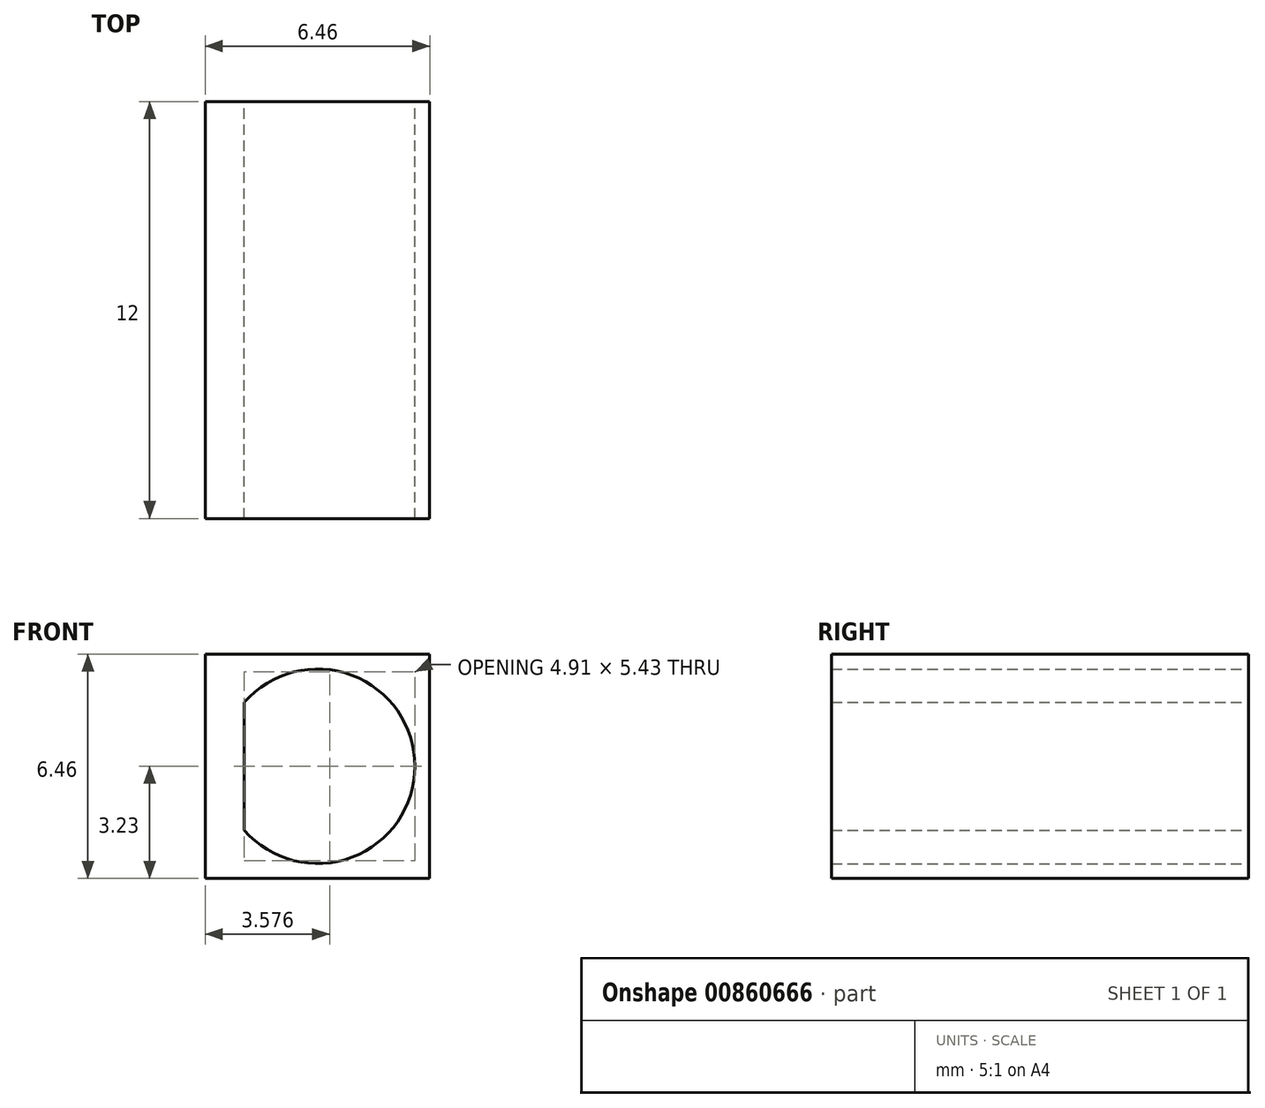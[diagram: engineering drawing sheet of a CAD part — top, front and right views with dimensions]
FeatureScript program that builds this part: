
annotation { "Feature Type Name" : "Feature", "Feature Type Description" : "" }
export const myFeature = defineFeature(function(context is Context, id is Id, definition is map)
    precondition{}
    {
        {
            var Q0;
            Q0=qCreatedBy(makeId("Front.planeOp"),FACE);
            var sketch = newSketch(context, id + "F0", { "sketchPlane" : qUnion([Q0])});
            skLineSegment(sketch, "E0.bottom", {"start": v(3.23, 3.23) * mm, "end": v(-3.23, 3.23) * mm});
            skLineSegment(sketch, "E0.top", {"start": v(3.23, -3.23) * mm, "end": v(-3.23, -3.23) * mm});
            skLineSegment(sketch, "E0.left", {"start": v(3.23, 3.23) * mm, "end": v(3.23, -3.23) * mm});
            skLineSegment(sketch, "E0.right", {"start": v(-3.23, 3.23) * mm, "end": v(-3.23, -3.23) * mm});
            skPoint(sketch, "E0.middle", {"position": v(0, 0) * mm});
            skSolve(sketch);
        }
        {
            var Q0;
            Q0=qCreatedBy(makeId("Front.planeOp"),FACE);
            var sketch = newSketch(context, id + "F1", { "sketchPlane" : qUnion([Q0])});
            skCircle(sketch, "E1", {"center": v(0, 0) * mm, "radius": 2.8 * mm});
            skSolve(sketch);
        }
        {
            var Q0;
            Q0 = qSketchRegion(id + "F0", true);
            extrude(context, id + "F2", {"entities" : qUnion([Q0]), "depth" : 12 * mm, "offsetDistance" : 25.4 * mm});
        }
        {
            var Q0;
            Q0 = qSketchRegion(id + "F1", true);
            extrude(context, id + "F3", {"entities" : qUnion([Q0]), "operationType" : NewBodyOperationType.REMOVE, "depth" : 12 * mm, "offsetDistance" : 25.4 * mm});
        }
        {
            var Q0;
            Q0=qCreatedBy(makeId("Front.planeOp"),FACE);
            var sketch = newSketch(context, id + "F4", { "sketchPlane" : qUnion([Q0])});
            skLineSegment(sketch, "E2", {"start": v(-2.9, 3.13) * mm, "end": v(-2.9, -2.79) * mm});
            skLineSegment(sketch, "E3", {"start": v(-2.9, -2.79) * mm, "end": v(-2.1, -2.79) * mm});
            skLineSegment(sketch, "E4", {"start": v(-2.1, -2.79) * mm, "end": v(-2.1, 3.13) * mm});
            skLineSegment(sketch, "E5", {"start": v(-2.1, 3.13) * mm, "end": v(-2.9, 3.13) * mm});
            skSolve(sketch);
        }
        {
            var Q0;
            Q0 = qSketchRegion(id + "F4", true);
            extrude(context, id + "F5", {"entities" : qUnion([Q0]), "operationType" : NewBodyOperationType.ADD, "depth" : 12 * mm, "offsetDistance" : 25.4 * mm});
        }
    });
